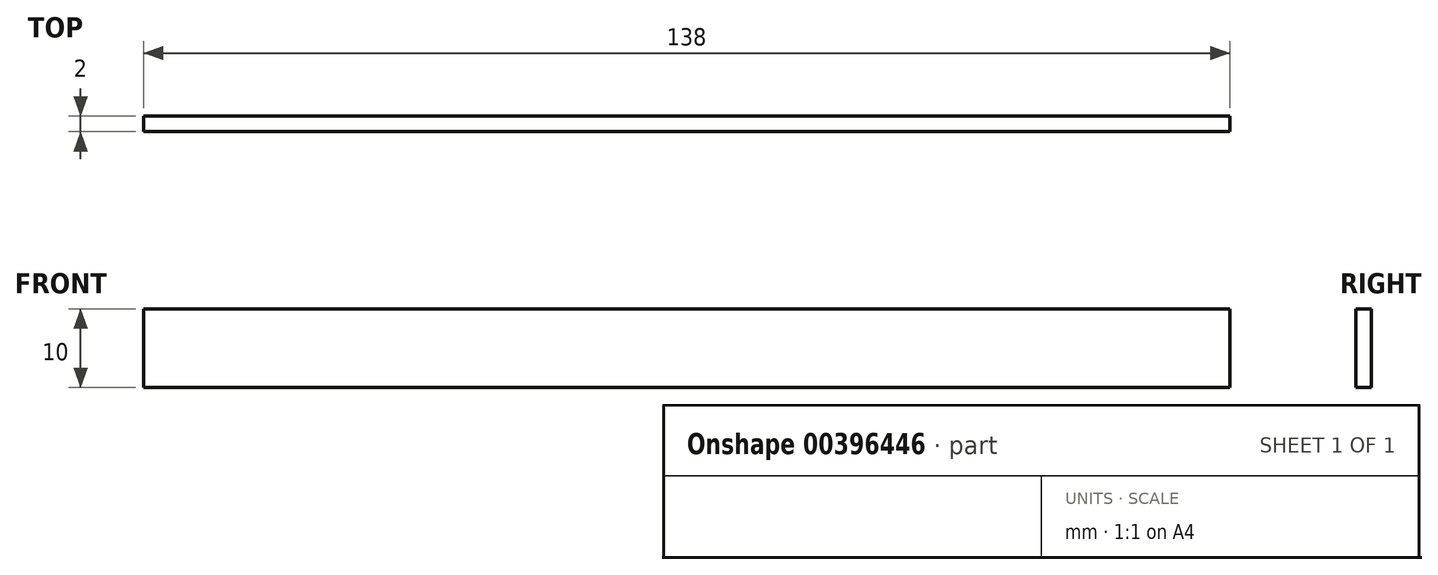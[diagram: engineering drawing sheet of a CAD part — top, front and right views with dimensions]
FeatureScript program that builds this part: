
annotation { "Feature Type Name" : "Feature", "Feature Type Description" : "" }
export const myFeature = defineFeature(function(context is Context, id is Id, definition is map)
    precondition{}
    {
        {
            var Q0;
            Q0=qCreatedBy(makeId("Front.planeOp"),FACE);
            var sketch = newSketch(context, id + "F0", { "sketchPlane" : qUnion([Q0])});
            skLineSegment(sketch, "E0.bottom", {"start": v(-93.73, 23.14) * mm, "end": v(44.27, 23.14) * mm});
            skLineSegment(sketch, "E0.top", {"start": v(-93.73, 13.14) * mm, "end": v(44.27, 13.14) * mm});
            skLineSegment(sketch, "E0.left", {"start": v(-93.73, 23.14) * mm, "end": v(-93.73, 13.14) * mm});
            skLineSegment(sketch, "E0.right", {"start": v(44.27, 23.14) * mm, "end": v(44.27, 13.14) * mm});
            skSolve(sketch);
        }
        {
            var Q0;
            Q0=makeQuery(id+"F0.imprint","IMPRINT",FACE,{"disambiguationData":[TD([[makeQuery(id+"F0.imprint","IMPRINT",EDGE,{"derivedFrom":sQuery(id+"F0.wireOp",EDGE,"E0.bottom")}),-1.0]])]});
            extrude(context, id + "F1", {"entities" : qUnion([Q0]), "depth" : 2 * mm});
        }
    });
